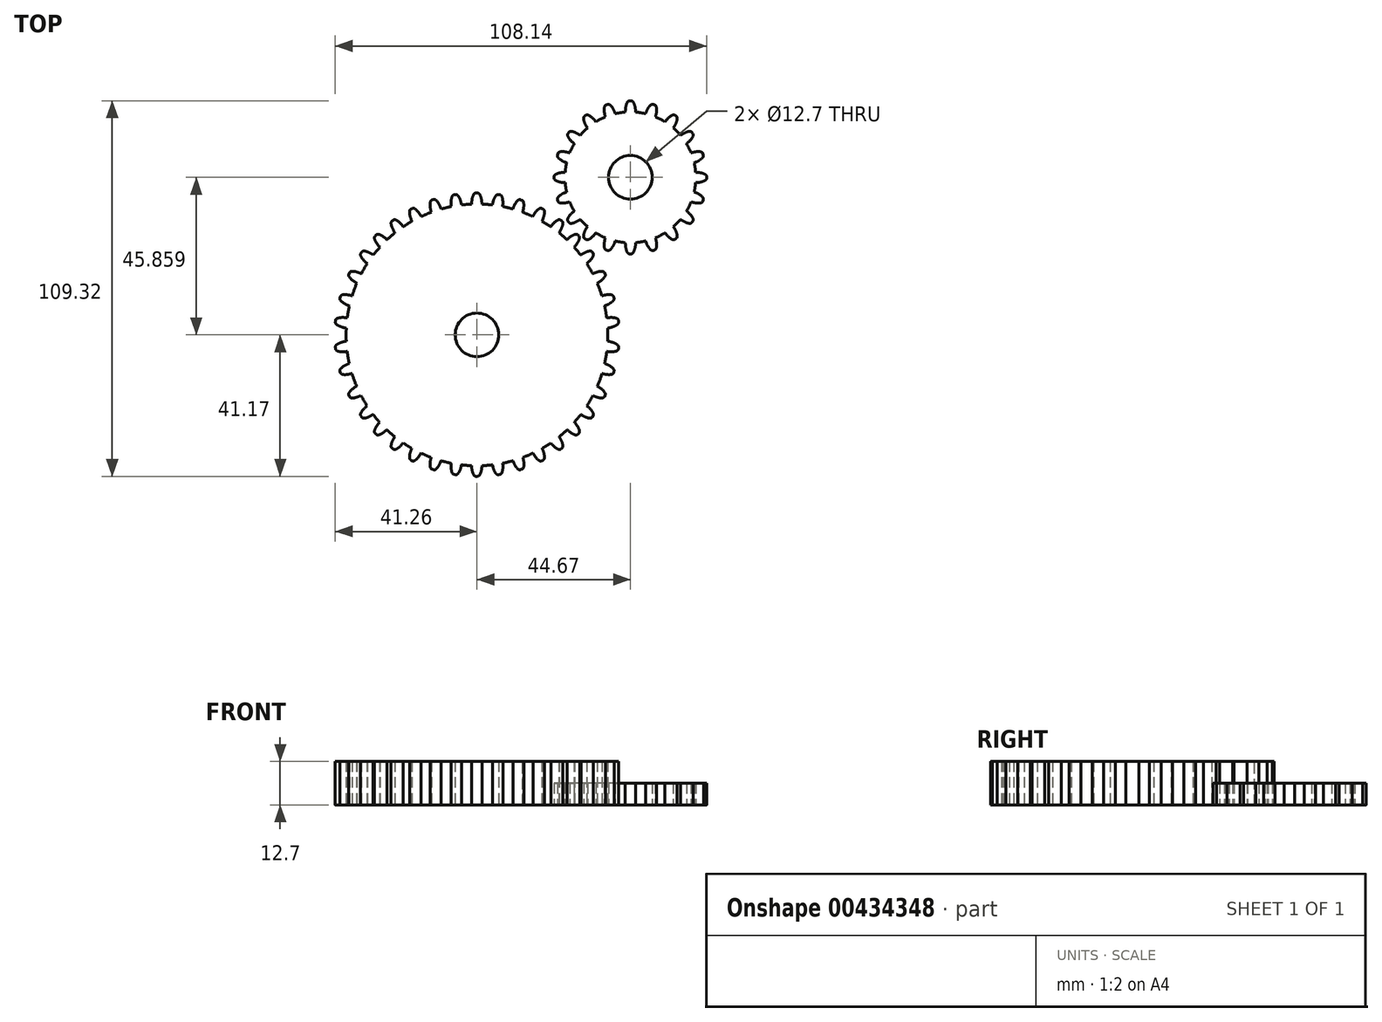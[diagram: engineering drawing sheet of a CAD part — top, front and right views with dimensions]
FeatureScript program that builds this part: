
annotation { "Feature Type Name" : "Feature", "Feature Type Description" : "" }
export const myFeature = defineFeature(function(context is Context, id is Id, definition is map)
    precondition{}
    {
        {
            var Q0;
            Q0=qCreatedBy(makeId("Top.planeOp"),FACE);
            var sketch = newSketch(context, id + "F0", { "sketchPlane" : qUnion([Q0])});
            skCircle(sketch, "E0", {"center": v(0, 0) * mm, "radius": 38.1 * mm});
            skCircle(sketch, "E1", {"center": v(0, 0) * mm, "radius": 6.35 * mm});
            skEllipticalArc(sketch, "E2", {});
            skLineSegment(sketch, "E3", {"start": v(12.68, 39.34) * mm, "end": v(13.04, 39.21) * mm});
            skPoint(sketch, "E4.visualSharp", {"position": v(12.33, 39.46) * mm});
            skPoint(sketch, "E5.visualSharp", {"position": v(13.37, 39.1) * mm});
            skArc(sketch, "E5.filletArc", {"start": v(13.53, 38.69) * mm, "mid": v(13.35, 39.01) * mm, "end": v(13.04, 39.21) * mm});
            skArc(sketch, "E6.filletArc", {"start": v(12.68, 39.34) * mm, "mid": v(12.29, 39.37) * mm, "end": v(11.94, 39.2) * mm});
            skLineSegment(sketch, "E7", {"start": v(10.43, 36.57) * mm, "end": v(13.3, 35.7) * mm});
            skEllipticalArc(sketch, "E8", {});
            skLineSegment(sketch, "E9", {"start": v(18.9, 36.8) * mm, "end": v(19.22, 36.63) * mm});
            skPoint(sketch, "E10.visualSharp", {"position": v(18.6, 36.96) * mm});
            skArc(sketch, "E11.filletArc", {"start": v(19.62, 36.05) * mm, "mid": v(19.5, 36.39) * mm, "end": v(19.22, 36.63) * mm});
            skArc(sketch, "E12.filletArc", {"start": v(18.9, 36.8) * mm, "mid": v(18.53, 36.89) * mm, "end": v(18.16, 36.78) * mm});
            skLineSegment(sketch, "E13", {"start": v(16.24, 34.4) * mm, "end": v(18.93, 33.1) * mm});
            skEllipticalArc(sketch, "E14", {});
            skLineSegment(sketch, "E15", {"start": v(24.42, 33.38) * mm, "end": v(24.72, 33.15) * mm});
            skPoint(sketch, "E16.visualSharp", {"position": v(24.12, 33.6) * mm});
            skPoint(sketch, "E17.visualSharp", {"position": v(25, 32.94) * mm});
            skArc(sketch, "E17.filletArc", {"start": v(25.02, 32.5) * mm, "mid": v(24.95, 32.87) * mm, "end": v(24.72, 33.15) * mm});
            skArc(sketch, "E18.filletArc", {"start": v(24.42, 33.38) * mm, "mid": v(24.05, 33.53) * mm, "end": v(23.67, 33.48) * mm});
            skLineSegment(sketch, "E19", {"start": v(21.43, 31.44) * mm, "end": v(23.88, 29.73) * mm});
            skEllipticalArc(sketch, "E20", {});
            skLineSegment(sketch, "E21", {"start": v(33.57, 24.1) * mm, "end": v(33.8, 23.79) * mm});
            skPoint(sketch, "E22.visualSharp", {"position": v(33.36, 24.4) * mm});
            skPoint(sketch, "E23.visualSharp", {"position": v(33.99, 23.5) * mm});
            skArc(sketch, "E23.filletArc", {"start": v(33.88, 23.08) * mm, "mid": v(33.92, 23.44) * mm, "end": v(33.8, 23.79) * mm});
            skArc(sketch, "E24.filletArc", {"start": v(33.57, 24.1) * mm, "mid": v(33.27, 24.35) * mm, "end": v(32.89, 24.42) * mm});
            skLineSegment(sketch, "E25", {"start": v(30.13, 23.18) * mm, "end": v(31.94, 20.79) * mm});
            skEllipticalArc(sketch, "E26", {});
            skLineSegment(sketch, "E27", {"start": v(37.13, 18.09) * mm, "end": v(37.3, 17.75) * mm});
            skPoint(sketch, "E28.visualSharp", {"position": v(36.97, 18.42) * mm});
            skPoint(sketch, "E29.visualSharp", {"position": v(37.45, 17.43) * mm});
            skArc(sketch, "E29.filletArc", {"start": v(37.28, 17.03) * mm, "mid": v(37.38, 17.38) * mm, "end": v(37.3, 17.75) * mm});
            skArc(sketch, "E30.filletArc", {"start": v(37.13, 18.09) * mm, "mid": v(36.88, 18.38) * mm, "end": v(36.5, 18.51) * mm});
            skLineSegment(sketch, "E31", {"start": v(33.59, 17.72) * mm, "end": v(35, 15.07) * mm});
            skEllipticalArc(sketch, "E32", {});
            skLineSegment(sketch, "E33", {"start": v(39.78, 11.13) * mm, "end": v(39.9, 10.77) * mm});
            skPoint(sketch, "E34.visualSharp", {"position": v(39.68, 11.48) * mm});
            skPoint(sketch, "E35.visualSharp", {"position": v(40, 10.44) * mm});
            skArc(sketch, "E35.filletArc", {"start": v(39.76, 10.07) * mm, "mid": v(39.91, 10.4) * mm, "end": v(39.9, 10.77) * mm});
            skArc(sketch, "E36.filletArc", {"start": v(39.78, 11.13) * mm, "mid": v(39.58, 11.47) * mm, "end": v(39.23, 11.65) * mm});
            skLineSegment(sketch, "E37", {"start": v(36.23, 11.32) * mm, "end": v(37.2, 8.49) * mm});
            skPoint(sketch, "E38.visualSharp", {"position": v(-45.71, -0.07) * mm});
            skPoint(sketch, "E39", {"position": v(4.52, 37.83) * mm});
            skEllipticalArc(sketch, "E40", {});
            skLineSegment(sketch, "E41", {"start": v(6.28, 40.86) * mm, "end": v(6.66, 40.8) * mm});
            skPoint(sketch, "E42.visualSharp", {"position": v(5.92, 40.93) * mm});
            skPoint(sketch, "E43.visualSharp", {"position": v(7, 40.74) * mm});
            skArc(sketch, "E43.filletArc", {"start": v(7.22, 40.36) * mm, "mid": v(7, 40.65) * mm, "end": v(6.66, 40.8) * mm});
            skArc(sketch, "E44.filletArc", {"start": v(6.28, 40.86) * mm, "mid": v(5.9, 40.83) * mm, "end": v(5.57, 40.6) * mm});
            skLineSegment(sketch, "E45", {"start": v(4.5, 37.78) * mm, "end": v(7.47, 37.37) * mm});
            skPoint(sketch, "E46", {"position": v(0, 38.1) * mm});
            skPoint(sketch, "E47", {"position": v(10.46, 36.63) * mm});
            skPoint(sketch, "E48", {"position": v(16.3, 34.44) * mm});
            skPoint(sketch, "E49", {"position": v(21.46, 31.48) * mm});
            skPoint(sketch, "E50", {"position": v(26.2, 27.67) * mm});
            skEllipticalArc(sketch, "E51", {});
            skLineSegment(sketch, "E52", {"start": v(29.4, 29.07) * mm, "end": v(29.66, 28.8) * mm});
            skPoint(sketch, "E53.visualSharp", {"position": v(29.14, 29.34) * mm});
            skPoint(sketch, "E54.visualSharp", {"position": v(29.9, 28.55) * mm});
            skArc(sketch, "E54.filletArc", {"start": v(29.86, 28.11) * mm, "mid": v(29.85, 28.48) * mm, "end": v(29.66, 28.8) * mm});
            skArc(sketch, "E55.filletArc", {"start": v(29.4, 29.07) * mm, "mid": v(29.06, 29.28) * mm, "end": v(28.67, 29.29) * mm});
            skLineSegment(sketch, "E56", {"start": v(26.14, 27.63) * mm, "end": v(28.3, 25.55) * mm});
            skPoint(sketch, "E57", {"position": v(30.2, 23.23) * mm});
            skPoint(sketch, "E58", {"position": v(33.7, 17.79) * mm});
            skPoint(sketch, "E59", {"position": v(36.14, 12.08) * mm});
            skPoint(sketch, "E60", {"position": v(37.7, 5.5) * mm});
            skEllipticalArc(sketch, "E61", {});
            skLineSegment(sketch, "E62", {"start": v(-0.26, 41.32) * mm, "end": v(0.12, 41.32) * mm});
            skPoint(sketch, "E63.visualSharp", {"position": v(-0.63, 41.33) * mm});
            skPoint(sketch, "E64.visualSharp", {"position": v(0.46, 41.31) * mm});
            skArc(sketch, "E64.filletArc", {"start": v(0.74, 40.97) * mm, "mid": v(0.47, 41.22) * mm, "end": v(0.12, 41.32) * mm});
            skArc(sketch, "E65.filletArc", {"start": v(-0.26, 41.32) * mm, "mid": v(-0.64, 41.23) * mm, "end": v(-0.93, 40.96) * mm});
            skLineSegment(sketch, "E66", {"start": v(-1.54, 38) * mm, "end": v(1.45, 38.05) * mm});
            skEllipticalArc(sketch, "E67", {});
            skLineSegment(sketch, "E68", {"start": v(41.2, 4.2) * mm, "end": v(41.25, 3.83) * mm});
            skPoint(sketch, "E69.visualSharp", {"position": v(41.14, 4.57) * mm});
            skPoint(sketch, "E70.visualSharp", {"position": v(41.3, 3.48) * mm});
            skArc(sketch, "E70.filletArc", {"start": v(41, 3.15) * mm, "mid": v(41.21, 3.46) * mm, "end": v(41.25, 3.83) * mm});
            skArc(sketch, "E71.filletArc", {"start": v(41.2, 4.2) * mm, "mid": v(41.04, 4.56) * mm, "end": v(40.73, 4.8) * mm});
            skLineSegment(sketch, "E72", {"start": v(37.71, 4.95) * mm, "end": v(38.23, 2) * mm});
            skEllipticalArc(sketch, "E73.MirrorCS", {});
            skArc(sketch, "E74.MirrorCS", {"start": v(6.28, -40.71) * mm, "mid": v(5.9, -40.68) * mm, "end": v(5.57, -40.46) * mm});
            skLineSegment(sketch, "E75.MirrorCS", {"start": v(6.28, -40.71) * mm, "end": v(6.66, -40.65) * mm});
            skArc(sketch, "E76.MirrorCS", {"start": v(7.22, -40.2) * mm, "mid": v(7, -40.5) * mm, "end": v(6.66, -40.65) * mm});
            skEllipticalArc(sketch, "E77.MirrorCS", {});
            skLineSegment(sketch, "E78.MirrorCS", {"start": v(-0.26, -41.17) * mm, "end": v(0.12, -41.17) * mm});
            skArc(sketch, "E79.MirrorCS", {"start": v(-0.26, -41.17) * mm, "mid": v(-0.64, -41.08) * mm, "end": v(-0.93, -40.8) * mm});
            skArc(sketch, "E80.MirrorCS", {"start": v(0.74, -40.82) * mm, "mid": v(0.47, -41.07) * mm, "end": v(0.12, -41.17) * mm});
            skEllipticalArc(sketch, "E81.MirrorCS", {});
            skArc(sketch, "E82.MirrorCS", {"start": v(12.7, -39.25) * mm, "mid": v(12.32, -39.28) * mm, "end": v(11.96, -39.11) * mm});
            skLineSegment(sketch, "E83.MirrorCS", {"start": v(12.7, -39.25) * mm, "end": v(13.07, -39.13) * mm});
            skArc(sketch, "E84.MirrorCS", {"start": v(13.55, -38.6) * mm, "mid": v(13.38, -38.93) * mm, "end": v(13.07, -39.13) * mm});
            skEllipticalArc(sketch, "E85.MirrorCS", {});
            skPoint(sketch, "E86.MirrorP", {"position": v(18.6, -36.81) * mm});
            skArc(sketch, "E87.MirrorCS", {"start": v(18.9, -36.65) * mm, "mid": v(18.53, -36.73) * mm, "end": v(18.16, -36.63) * mm});
            skLineSegment(sketch, "E88.MirrorCS", {"start": v(18.9, -36.65) * mm, "end": v(19.22, -36.48) * mm});
            skArc(sketch, "E89.MirrorCS", {"start": v(19.62, -35.9) * mm, "mid": v(19.5, -36.24) * mm, "end": v(19.22, -36.48) * mm});
            skEllipticalArc(sketch, "E90.MirrorCS", {});
            skArc(sketch, "E91.MirrorCS", {"start": v(24.42, -33.23) * mm, "mid": v(24.05, -33.38) * mm, "end": v(23.67, -33.33) * mm});
            skLineSegment(sketch, "E92.MirrorCS", {"start": v(24.42, -33.23) * mm, "end": v(24.72, -33) * mm});
            skPoint(sketch, "E93.MirrorP", {"position": v(25, -32.8) * mm});
            skArc(sketch, "E94.MirrorCS", {"start": v(25.02, -32.35) * mm, "mid": v(24.95, -32.71) * mm, "end": v(24.72, -33) * mm});
            skEllipticalArc(sketch, "E95.MirrorCS", {});
            skArc(sketch, "E96.MirrorCS", {"start": v(29.4, -28.92) * mm, "mid": v(29.06, -29.13) * mm, "end": v(28.67, -29.13) * mm});
            skLineSegment(sketch, "E97.MirrorCS", {"start": v(29.4, -28.92) * mm, "end": v(29.66, -28.65) * mm});
            skPoint(sketch, "E98.MirrorP", {"position": v(29.9, -28.4) * mm});
            skArc(sketch, "E99.MirrorCS", {"start": v(29.86, -27.96) * mm, "mid": v(29.85, -28.33) * mm, "end": v(29.66, -28.65) * mm});
            skEllipticalArc(sketch, "E100.MirrorCS", {});
            skArc(sketch, "E101.MirrorCS", {"start": v(33.57, -23.95) * mm, "mid": v(33.27, -24.2) * mm, "end": v(32.89, -24.27) * mm});
            skLineSegment(sketch, "E102.MirrorCS", {"start": v(33.57, -23.95) * mm, "end": v(33.8, -23.63) * mm});
            skPoint(sketch, "E103.MirrorP", {"position": v(33.99, -23.35) * mm});
            skArc(sketch, "E104.MirrorCS", {"start": v(33.88, -22.92) * mm, "mid": v(33.92, -23.3) * mm, "end": v(33.8, -23.63) * mm});
            skLineSegment(sketch, "E105.MirrorCS", {"start": v(37.13, -17.94) * mm, "end": v(37.3, -17.6) * mm});
            skArc(sketch, "E106.MirrorCS", {"start": v(37.13, -17.94) * mm, "mid": v(36.88, -18.23) * mm, "end": v(36.5, -18.36) * mm});
            skEllipticalArc(sketch, "E107.MirrorCS", {});
            skPoint(sketch, "E108.MirrorP", {"position": v(37.45, -17.28) * mm});
            skArc(sketch, "E109.MirrorCS", {"start": v(37.28, -16.88) * mm, "mid": v(37.38, -17.23) * mm, "end": v(37.3, -17.6) * mm});
            skEllipticalArc(sketch, "E110.MirrorCS", {});
            skArc(sketch, "E111.MirrorCS", {"start": v(39.78, -10.98) * mm, "mid": v(39.58, -11.31) * mm, "end": v(39.23, -11.5) * mm});
            skLineSegment(sketch, "E112.MirrorCS", {"start": v(39.78, -10.98) * mm, "end": v(39.9, -10.62) * mm});
            skArc(sketch, "E113.MirrorCS", {"start": v(39.76, -9.91) * mm, "mid": v(39.91, -10.25) * mm, "end": v(39.9, -10.62) * mm});
            skArc(sketch, "E114.MirrorCS", {"start": v(41, -3) * mm, "mid": v(41.21, -3.3) * mm, "end": v(41.25, -3.68) * mm});
            skArc(sketch, "E115.MirrorCS", {"start": v(41.2, -4.05) * mm, "mid": v(41.04, -4.41) * mm, "end": v(40.73, -4.65) * mm});
            skLineSegment(sketch, "E116.MirrorCS", {"start": v(41.2, -4.05) * mm, "end": v(41.25, -3.68) * mm});
            skEllipticalArc(sketch, "E117.MirrorCS", {});
            skEllipticalArc(sketch, "E118.MirrorCS", {});
            skArc(sketch, "E119.MirrorCS", {"start": v(-6.28, -40.71) * mm, "mid": v(-5.9, -40.68) * mm, "end": v(-5.57, -40.46) * mm});
            skArc(sketch, "E120.MirrorCS", {"start": v(-7.22, -40.2) * mm, "mid": v(-7, -40.5) * mm, "end": v(-6.66, -40.65) * mm});
            skLineSegment(sketch, "E121.MirrorCS", {"start": v(-6.28, -40.71) * mm, "end": v(-6.66, -40.65) * mm});
            skEllipticalArc(sketch, "E122.MirrorCS", {});
            skArc(sketch, "E123.MirrorCS", {"start": v(-13.55, -38.6) * mm, "mid": v(-13.38, -38.93) * mm, "end": v(-13.07, -39.13) * mm});
            skArc(sketch, "E124.MirrorCS", {"start": v(-12.7, -39.25) * mm, "mid": v(-12.32, -39.28) * mm, "end": v(-11.96, -39.11) * mm});
            skLineSegment(sketch, "E125.MirrorCS", {"start": v(-12.7, -39.25) * mm, "end": v(-13.07, -39.13) * mm});
            skEllipticalArc(sketch, "E126.MirrorCS", {});
            skArc(sketch, "E127.MirrorCS", {"start": v(-19.62, -35.9) * mm, "mid": v(-19.5, -36.24) * mm, "end": v(-19.22, -36.48) * mm});
            skArc(sketch, "E128.MirrorCS", {"start": v(-18.9, -36.65) * mm, "mid": v(-18.53, -36.73) * mm, "end": v(-18.16, -36.63) * mm});
            skLineSegment(sketch, "E129.MirrorCS", {"start": v(-18.9, -36.65) * mm, "end": v(-19.22, -36.48) * mm});
            skEllipticalArc(sketch, "E130.MirrorCS", {});
            skArc(sketch, "E131.MirrorCS", {"start": v(-25.02, -32.35) * mm, "mid": v(-24.95, -32.71) * mm, "end": v(-24.72, -33) * mm});
            skArc(sketch, "E132.MirrorCS", {"start": v(-24.42, -33.23) * mm, "mid": v(-24.05, -33.38) * mm, "end": v(-23.67, -33.33) * mm});
            skLineSegment(sketch, "E133.MirrorCS", {"start": v(-24.42, -33.23) * mm, "end": v(-24.72, -33) * mm});
            skEllipticalArc(sketch, "E134.MirrorCS", {});
            skArc(sketch, "E135.MirrorCS", {"start": v(-29.86, -27.96) * mm, "mid": v(-29.85, -28.33) * mm, "end": v(-29.66, -28.65) * mm});
            skArc(sketch, "E136.MirrorCS", {"start": v(-29.4, -28.92) * mm, "mid": v(-29.06, -29.13) * mm, "end": v(-28.67, -29.13) * mm});
            skLineSegment(sketch, "E137.MirrorCS", {"start": v(-29.4, -28.92) * mm, "end": v(-29.66, -28.65) * mm});
            skEllipticalArc(sketch, "E138.MirrorCS", {});
            skArc(sketch, "E139.MirrorCS", {"start": v(-33.88, -22.92) * mm, "mid": v(-33.92, -23.3) * mm, "end": v(-33.8, -23.63) * mm});
            skArc(sketch, "E140.MirrorCS", {"start": v(-33.57, -23.95) * mm, "mid": v(-33.27, -24.2) * mm, "end": v(-32.89, -24.27) * mm});
            skLineSegment(sketch, "E141.MirrorCS", {"start": v(-33.57, -23.95) * mm, "end": v(-33.8, -23.63) * mm});
            skEllipticalArc(sketch, "E142.MirrorCS", {});
            skArc(sketch, "E143.MirrorCS", {"start": v(-37.28, -16.88) * mm, "mid": v(-37.38, -17.23) * mm, "end": v(-37.3, -17.6) * mm});
            skArc(sketch, "E144.MirrorCS", {"start": v(-37.13, -17.94) * mm, "mid": v(-36.88, -18.23) * mm, "end": v(-36.5, -18.36) * mm});
            skLineSegment(sketch, "E145.MirrorCS", {"start": v(-37.13, -17.94) * mm, "end": v(-37.3, -17.6) * mm});
            skEllipticalArc(sketch, "E146.MirrorCS", {});
            skArc(sketch, "E147.MirrorCS", {"start": v(-39.78, -10.98) * mm, "mid": v(-39.58, -11.31) * mm, "end": v(-39.23, -11.5) * mm});
            skArc(sketch, "E148.MirrorCS", {"start": v(-39.76, -9.91) * mm, "mid": v(-39.91, -10.25) * mm, "end": v(-39.9, -10.62) * mm});
            skEllipticalArc(sketch, "E149.MirrorCS", {});
            skArc(sketch, "E150.MirrorCS", {"start": v(-41.2, -4.05) * mm, "mid": v(-41.04, -4.41) * mm, "end": v(-40.73, -4.65) * mm});
            skLineSegment(sketch, "E151.MirrorCS", {"start": v(-41.2, -4.05) * mm, "end": v(-41.25, -3.68) * mm});
            skArc(sketch, "E152.MirrorCS", {"start": v(-41, -3) * mm, "mid": v(-41.21, -3.3) * mm, "end": v(-41.25, -3.68) * mm});
            skEllipticalArc(sketch, "E153.MirrorCS", {});
            skPoint(sketch, "E154.MirrorP", {"position": v(-41.3, 3.48) * mm});
            skArc(sketch, "E155.MirrorCS", {"start": v(-41, 3.15) * mm, "mid": v(-41.21, 3.46) * mm, "end": v(-41.25, 3.83) * mm});
            skLineSegment(sketch, "E156.MirrorCS", {"start": v(-41.2, 4.2) * mm, "end": v(-41.25, 3.83) * mm});
            skArc(sketch, "E157.MirrorCS", {"start": v(-41.2, 4.2) * mm, "mid": v(-41.04, 4.56) * mm, "end": v(-40.73, 4.8) * mm});
            skEllipticalArc(sketch, "E158.MirrorCS", {});
            skArc(sketch, "E159.MirrorCS", {"start": v(-39.76, 10.07) * mm, "mid": v(-39.91, 10.4) * mm, "end": v(-39.9, 10.77) * mm});
            skLineSegment(sketch, "E160.MirrorCS", {"start": v(-39.78, 11.13) * mm, "end": v(-39.9, 10.77) * mm});
            skArc(sketch, "E161.MirrorCS", {"start": v(-39.78, 11.13) * mm, "mid": v(-39.58, 11.47) * mm, "end": v(-39.23, 11.65) * mm});
            skEllipticalArc(sketch, "E162.MirrorCS", {});
            skArc(sketch, "E163.MirrorCS", {"start": v(-37.28, 17.03) * mm, "mid": v(-37.38, 17.38) * mm, "end": v(-37.3, 17.75) * mm});
            skLineSegment(sketch, "E164.MirrorCS", {"start": v(-37.13, 18.09) * mm, "end": v(-37.3, 17.75) * mm});
            skArc(sketch, "E165.MirrorCS", {"start": v(-37.13, 18.09) * mm, "mid": v(-36.88, 18.38) * mm, "end": v(-36.5, 18.51) * mm});
            skEllipticalArc(sketch, "E166.MirrorCS", {});
            skArc(sketch, "E167.MirrorCS", {"start": v(-33.88, 23.08) * mm, "mid": v(-33.92, 23.44) * mm, "end": v(-33.8, 23.79) * mm});
            skLineSegment(sketch, "E168.MirrorCS", {"start": v(-33.57, 24.1) * mm, "end": v(-33.8, 23.79) * mm});
            skArc(sketch, "E169.MirrorCS", {"start": v(-33.57, 24.1) * mm, "mid": v(-33.27, 24.35) * mm, "end": v(-32.89, 24.42) * mm});
            skEllipticalArc(sketch, "E170.MirrorCS", {});
            skArc(sketch, "E171.MirrorCS", {"start": v(-29.86, 28.11) * mm, "mid": v(-29.85, 28.48) * mm, "end": v(-29.66, 28.8) * mm});
            skLineSegment(sketch, "E172.MirrorCS", {"start": v(-29.4, 29.07) * mm, "end": v(-29.66, 28.8) * mm});
            skArc(sketch, "E173.MirrorCS", {"start": v(-29.4, 29.07) * mm, "mid": v(-29.06, 29.28) * mm, "end": v(-28.67, 29.29) * mm});
            skEllipticalArc(sketch, "E174.MirrorCS", {});
            skArc(sketch, "E175.MirrorCS", {"start": v(-25.02, 32.5) * mm, "mid": v(-24.95, 32.87) * mm, "end": v(-24.72, 33.15) * mm});
            skLineSegment(sketch, "E176.MirrorCS", {"start": v(-24.42, 33.38) * mm, "end": v(-24.72, 33.15) * mm});
            skArc(sketch, "E177.MirrorCS", {"start": v(-24.42, 33.38) * mm, "mid": v(-24.05, 33.53) * mm, "end": v(-23.67, 33.48) * mm});
            skEllipticalArc(sketch, "E178.MirrorCS", {});
            skArc(sketch, "E179.MirrorCS", {"start": v(-19.62, 36.05) * mm, "mid": v(-19.5, 36.39) * mm, "end": v(-19.22, 36.63) * mm});
            skLineSegment(sketch, "E180.MirrorCS", {"start": v(-18.9, 36.8) * mm, "end": v(-19.22, 36.63) * mm});
            skArc(sketch, "E181.MirrorCS", {"start": v(-18.9, 36.8) * mm, "mid": v(-18.53, 36.89) * mm, "end": v(-18.16, 36.78) * mm});
            skEllipticalArc(sketch, "E182.MirrorCS", {});
            skArc(sketch, "E183.MirrorCS", {"start": v(-13.55, 38.76) * mm, "mid": v(-13.38, 39.08) * mm, "end": v(-13.07, 39.28) * mm});
            skLineSegment(sketch, "E184.MirrorCS", {"start": v(-12.7, 39.4) * mm, "end": v(-13.07, 39.28) * mm});
            skArc(sketch, "E185.MirrorCS", {"start": v(-12.7, 39.4) * mm, "mid": v(-12.32, 39.43) * mm, "end": v(-11.96, 39.26) * mm});
            skEllipticalArc(sketch, "E186.MirrorCS", {});
            skArc(sketch, "E187.MirrorCS", {"start": v(-7.22, 40.36) * mm, "mid": v(-7, 40.65) * mm, "end": v(-6.66, 40.8) * mm});
            skLineSegment(sketch, "E188.MirrorCS", {"start": v(-6.28, 40.86) * mm, "end": v(-6.66, 40.8) * mm});
            skArc(sketch, "E189.MirrorCS", {"start": v(-6.28, 40.86) * mm, "mid": v(-5.9, 40.83) * mm, "end": v(-5.57, 40.6) * mm});
            skLineSegment(sketch, "E190", {"start": v(-39.9, -10.62) * mm, "end": v(-39.78, -10.98) * mm});
            const initialGuessF0  = {"E2": [0.01186746590526298, 0.036133459957926904, 0.9565221208926966, -0.29165978852583985, 0.0014986000688646897, 0.0035390805472536617, 2.1566096616366126, 0.9748157687295604], "E8": [0.017585702386777147, 0.03374703845333271, 0.8991201033352045, -0.4377019988285309, 0.0014986000000007816, 0.003539080620550978, 2.1409023225018835, 0.9908088013620491], "E14": [0.02265578287977473, 0.03058570050431115, 0.819578764825096, -0.5729665332702865, 0.0014985999999604874, 0.0035390806203384963, 2.156609722361633, 0.974815710010029], "E20": [0.031033398799110372, 0.021983045095617812, 0.6024093289154265, -0.7981873216455305, 0.0014986000000000005, 0.0035390806205390707, 2.1566097223429517, 0.974815710028964], "E26": [0.034294476878703864, 0.01639607277429761, 0.4701286637719916, -0.8825978923042824, 0.0014986000000000005, 0.0035390806205390707, 2.1566097223429397, 0.9748157100289685], "E32": [0.036714569503235456, 0.009905693299014778, 0.32627187065891905, -0.9452759736800305, 0.0014985999847553029, 0.003539080625213695, 2.1566097285726453, 0.9748157042875452], "E40": [0.005982244381583665, 0.03757325514283656, 0.9903713893188204, -0.13843594626652975, 0.0014985999999950434, 0.0035390806205121863, 2.156609722345128, 0.9748157100267223], "E51": [0.02722062515224479, 0.026587915261583314, 0.7198566770990191, -0.6941227300960245, 0.0014985999999683702, 0.003539080620359171, 2.1566097223570546, 0.9748157100144512], "E61": [-4.473054053318043e-05, 0.03802693754338048, 0.99983442728575, 0.018196648432512064, 0.0014986000000000983, 0.0035390806205391036, 2.156609722343001, 0.9748157100289072], "E67": [0.03797341145007212, 0.003471938573619611, 0.1743811812559528, -0.9846782233926872, 0.0014985999999967946, 0.003539080620539968, 2.15660972234474, 0.9748157100274488], "E73.MirrorCS": [0.005982244381583665, -0.037421951624719965, 0.9903713893188204, 0.13843594626652975, 0.0014985999999950434, 0.0035390806205121863, 5.308369597152864, 4.126575584834459], "E77.MirrorCS": [-4.473054053318043e-05, -0.037875634025263887, 0.99983442728575, -0.018196648432512064, 0.0014986000000000983, 0.0035390806205391036, 5.308369597150679, 4.126575584836585], "E81.MirrorCS": [0.011894871004150282, -0.03605066825344335, 0.9565221208926966, 0.29165978852583985, 0.0014985999999839522, 0.0035390806204531537, 5.3083695971582525, 4.126575584829374], "E85.MirrorCS": [0.017585702386777147, -0.033595734935216115, 0.8991201033352045, 0.4377019988285309, 0.0014986000000007816, 0.003539080620550978, 5.292376505817537, 4.142282984677703], "E85.MirrorCS": [0.017585702386777147, -0.033595734935216115, 0.8991201033352045, 0.4377019988285309, 0.0014986000000007816, 0.003539080620550978, 5.292376505817537, 4.142282984677703], "E85.MirrorCS": [0.017585702386777147, -0.033595734935216115, 0.8991201033352045, 0.4377019988285309, 0.0014986000000007816, 0.003539080620550978, 5.292376505817537, 4.142282984677703], "E90.MirrorCS": [0.02265578287977473, -0.030434396986194552, 0.819578764825096, 0.5729665332702865, 0.0014985999999604874, 0.0035390806203384963, 5.308369597169592, 4.126575584817891], "E95.MirrorCS": [0.0272206251522448, -0.02643661174346671, 0.7198566770990189, 0.6941227300960248, 0.0014985999999683702, 0.003539080620359171, 5.308369597165132, 4.126575584822529], "E100.MirrorCS": [0.031033398799110372, -0.021831741577501215, 0.6024093289154265, 0.7981873216455305, 0.0014986000000000005, 0.0035390806205390707, 5.308369597150622, 4.126575584836635], "E107.MirrorCS": [0.034294476878703864, -0.016244769256181013, 0.4701286637719916, 0.8825978923042824, 0.0014986000000000005, 0.0035390806205390707, 5.308369597150618, 4.1265755848366465], "E110.MirrorCS": [0.036714569503235456, -0.009754389780898182, 0.32627187065891905, 0.9452759736800305, 0.0014985999847553029, 0.003539080625213695, 5.308369602892046, 4.126575578606946], "E117.MirrorCS": [0.03797341145007212, -0.0033206350555030125, 0.1743811812559528, 0.9846782233926872, 0.0014985999999967946, 0.003539080620539968, 5.308369597152129, 4.126575584834848], "E117.MirrorCS": [0.03797341145007212, -0.0033206350555030125, 0.1743811812559528, 0.9846782233926872, 0.0014985999999967946, 0.003539080620539968, 5.308369597152129, 4.126575584834848], "E118.MirrorCS": [-0.005982244381583665, -0.037421951624719965, -0.9903713893188204, 0.13843594626652975, 0.0014985999999950434, 0.0035390806205121863, 2.1566097223451273, 0.9748157100267223], "E122.MirrorCS": [-0.011894871004150282, -0.03605066825344335, -0.9565221208926966, 0.29165978852583985, 0.0014985999999839522, 0.0035390806204531537, 2.156609722350213, 0.9748157100213337], "E126.MirrorCS": [-0.017585702386777147, -0.033595734935216115, -0.8991201033352045, 0.4377019988285309, 0.0014986000000007816, 0.003539080620550978, 2.1409023225018835, 0.9908088013620491], "E130.MirrorCS": [-0.02265578287977473, -0.030434396986194552, -0.819578764825096, 0.5729665332702865, 0.0014985999999604874, 0.0035390806203384963, 2.1566097223616953, 0.9748157100099935], "E134.MirrorCS": [-0.0272206251522448, -0.02643661174346671, -0.7198566770990189, 0.6941227300960248, 0.0014985999999683702, 0.003539080620359171, 2.156609722357058, 0.9748157100144548], "E138.MirrorCS": [-0.031033398799110372, -0.021831741577501215, -0.6024093289154265, 0.7981873216455305, 0.0014986000000000005, 0.0035390806205390707, 2.1566097223429512, 0.974815710028964], "E142.MirrorCS": [-0.034294476878703864, -0.016244769256181013, -0.4701286637719916, 0.8825978923042824, 0.0014986000000000005, 0.0035390806205390707, 2.1566097223429397, 0.9748157100289685], "E146.MirrorCS": [-0.036714569503235456, -0.009754389780898182, -0.32627187065891905, 0.9452759736800305, 0.0014985999847553029, 0.003539080625213695, 2.156609728572639, 0.9748157042875407], "E149.MirrorCS": [-0.03797341145007212, -0.0033206350555030125, -0.1743811812559528, 0.9846782233926872, 0.0014985999999967946, 0.003539080620539968, 2.1566097223447365, 0.9748157100274568], "E153.MirrorCS": [-0.03797341145007212, 0.003471938573619611, -0.1743811812559528, -0.9846782233926872, 0.0014985999999967946, 0.003539080620539968, 5.308369597152129, 4.12657558483485], "E158.MirrorCS": [-0.036714569503235456, 0.009905693299014778, -0.32627187065891905, -0.9452759736800305, 0.0014985999847553029, 0.003539080625213695, 5.308369602892045, 4.1265755786069445], "E162.MirrorCS": [-0.034294476878703864, 0.01639607277429761, -0.4701286637719916, -0.8825978923042824, 0.0014986000000000005, 0.0035390806205390707, 5.308369597150618, 4.1265755848366465], "E166.MirrorCS": [-0.031033398799110372, 0.021983045095617812, -0.6024093289154265, -0.7981873216455305, 0.0014986000000000005, 0.0035390806205390707, 5.308369597150622, 4.126575584836635], "E170.MirrorCS": [-0.02722062515224479, 0.026587915261583314, -0.7198566770990191, -0.6941227300960245, 0.0014985999999683702, 0.003539080620359171, 5.308369597165135, 4.126575584822532], "E174.MirrorCS": [-0.02265578287977473, 0.03058570050431115, -0.819578764825096, -0.5729665332702865, 0.0014985999999604874, 0.0035390806203384963, 5.308369597169592, 4.126575584817891], "E178.MirrorCS": [-0.017585702386777147, 0.03374703845333271, -0.8991201033352045, -0.4377019988285309, 0.0014986000000007816, 0.003539080620550978, 5.292376505817537, 4.142282984677703], "E182.MirrorCS": [-0.011894871004150282, 0.03620197177155995, -0.9565221208926966, -0.29165978852583985, 0.0014985999999839522, 0.0035390806204531537, 5.3083695971582525, 4.126575584829374], "E186.MirrorCS": [-0.005982244381583665, 0.03757325514283656, -0.9903713893188204, -0.13843594626652975, 0.0014985999999950434, 0.0035390806205121863, 5.308369597152864, 4.126575584834459]};
            skSetInitialGuess(sketch, initialGuessF0);
            skSolve(sketch);
        }
        {
            var Q0;
            Q0 = qSketchRegion(id + "F0", true);
            extrude(context, id + "F1", {"entities" : qUnion([Q0]), "depth" : 12.7 * mm});
        }
        {
            var Q0;
            Q0=qCreatedBy(makeId("Top.planeOp"),FACE);
            var sketch = newSketch(context, id + "F2", { "sketchPlane" : qUnion([Q0])});
            skCircle(sketch, "E191", {"center": v(44.67, 45.86) * mm, "radius": 19.05 * mm});
            skCircle(sketch, "E192", {"center": v(44.67, 45.86) * mm, "radius": 6.35 * mm});
            skEllipticalArc(sketch, "E193", {});
            skLineSegment(sketch, "E194", {"start": v(44.48, 68.15) * mm, "end": v(44.86, 68.14) * mm});
            skPoint(sketch, "E195.visualSharp", {"position": v(44.11, 68.16) * mm});
            skPoint(sketch, "E196.visualSharp", {"position": v(45.2, 68.14) * mm});
            skArc(sketch, "E196.filletArc", {"start": v(45.49, 67.8) * mm, "mid": v(45.22, 68.05) * mm, "end": v(44.86, 68.14) * mm});
            skArc(sketch, "E197.filletArc", {"start": v(44.48, 68.15) * mm, "mid": v(44.1, 68.06) * mm, "end": v(43.82, 67.79) * mm});
            skLineSegment(sketch, "E198", {"start": v(43.2, 64.83) * mm, "end": v(46.2, 64.88) * mm});
            skEllipticalArc(sketch, "E199", {});
            skLineSegment(sketch, "E200", {"start": v(51.34, 67.11) * mm, "end": v(51.7, 66.99) * mm});
            skPoint(sketch, "E201.visualSharp", {"position": v(51, 67.23) * mm});
            skPoint(sketch, "E202.visualSharp", {"position": v(52.03, 66.88) * mm});
            skArc(sketch, "E202.filletArc", {"start": v(52.19, 66.47) * mm, "mid": v(52.01, 66.79) * mm, "end": v(51.7, 66.99) * mm});
            skArc(sketch, "E203.filletArc", {"start": v(51.34, 67.11) * mm, "mid": v(50.95, 67.14) * mm, "end": v(50.6, 66.97) * mm});
            skLineSegment(sketch, "E204", {"start": v(49.1, 64.35) * mm, "end": v(51.96, 63.47) * mm});
            skEllipticalArc(sketch, "E205", {});
            skLineSegment(sketch, "E206", {"start": v(57.7, 63.9) * mm, "end": v(58, 63.67) * mm});
            skPoint(sketch, "E207.visualSharp", {"position": v(57.41, 64.12) * mm});
            skPoint(sketch, "E208.visualSharp", {"position": v(58.29, 63.46) * mm});
            skArc(sketch, "E208.filletArc", {"start": v(58.31, 63.02) * mm, "mid": v(58.24, 63.38) * mm, "end": v(58, 63.67) * mm});
            skArc(sketch, "E209.filletArc", {"start": v(57.7, 63.9) * mm, "mid": v(57.34, 64.05) * mm, "end": v(56.95, 64) * mm});
            skLineSegment(sketch, "E210", {"start": v(54.72, 61.96) * mm, "end": v(57.17, 60.24) * mm});
            skEllipticalArc(sketch, "E211", {});
            skLineSegment(sketch, "E212", {"start": v(65.8, 52.77) * mm, "end": v(65.9, 52.4) * mm});
            skPoint(sketch, "E213.visualSharp", {"position": v(65.69, 53.12) * mm});
            skPoint(sketch, "E214.visualSharp", {"position": v(66.01, 52.08) * mm});
            skArc(sketch, "E214.filletArc", {"start": v(65.78, 51.7) * mm, "mid": v(65.93, 52.04) * mm, "end": v(65.9, 52.4) * mm});
            skArc(sketch, "E215.filletArc", {"start": v(65.8, 52.77) * mm, "mid": v(65.59, 53.1) * mm, "end": v(65.24, 53.29) * mm});
            skLineSegment(sketch, "E216", {"start": v(62.24, 52.94) * mm, "end": v(63.23, 50.12) * mm});
            skPoint(sketch, "E217", {"position": v(49.2, 64.68) * mm});
            skPoint(sketch, "E218", {"position": v(54.96, 62.3) * mm});
            skPoint(sketch, "E219", {"position": v(59.4, 58.24) * mm});
            skPoint(sketch, "E220", {"position": v(62.5, 53) * mm});
            skEllipticalArc(sketch, "E221", {});
            skLineSegment(sketch, "E222", {"start": v(66.88, 46.03) * mm, "end": v(66.88, 45.65) * mm});
            skPoint(sketch, "E223.visualSharp", {"position": v(66.89, 46.4) * mm});
            skPoint(sketch, "E224.visualSharp", {"position": v(66.87, 45.3) * mm});
            skArc(sketch, "E224.filletArc", {"start": v(66.53, 45.03) * mm, "mid": v(66.78, 45.3) * mm, "end": v(66.88, 45.65) * mm});
            skArc(sketch, "E225.filletArc", {"start": v(66.88, 46.03) * mm, "mid": v(66.79, 46.41) * mm, "end": v(66.52, 46.7) * mm});
            skLineSegment(sketch, "E226", {"start": v(63.56, 47.31) * mm, "end": v(63.61, 44.32) * mm});
            skEllipticalArc(sketch, "E227.MirrorCS", {});
            skArc(sketch, "E228.MirrorCS", {"start": v(65.78, 40.01) * mm, "mid": v(65.93, 39.68) * mm, "end": v(65.9, 39.31) * mm});
            skLineSegment(sketch, "E229.MirrorCS", {"start": v(65.8, 38.95) * mm, "end": v(65.9, 39.31) * mm});
            skArc(sketch, "E230.MirrorCS", {"start": v(65.8, 38.95) * mm, "mid": v(65.59, 38.62) * mm, "end": v(65.24, 38.43) * mm});
            skEllipticalArc(sketch, "E231.MirrorCS", {});
            skPoint(sketch, "E232.MirrorP", {"position": v(38.35, 67.23) * mm});
            skArc(sketch, "E233.MirrorCS", {"start": v(38, 67.11) * mm, "mid": v(38.39, 67.14) * mm, "end": v(38.74, 66.97) * mm});
            skLineSegment(sketch, "E234.MirrorCS", {"start": v(38, 67.11) * mm, "end": v(37.64, 66.99) * mm});
            skArc(sketch, "E235.MirrorCS", {"start": v(37.15, 66.47) * mm, "mid": v(37.33, 66.79) * mm, "end": v(37.64, 66.99) * mm});
            skEllipticalArc(sketch, "E236.MirrorCS", {});
            skArc(sketch, "E237.MirrorCS", {"start": v(31.64, 63.9) * mm, "mid": v(32, 64.05) * mm, "end": v(32.39, 64) * mm});
            skEllipticalArc(sketch, "E238.MirrorCS", {});
            skArc(sketch, "E239.MirrorCS", {"start": v(58.31, 28.7) * mm, "mid": v(58.24, 28.34) * mm, "end": v(58, 28.05) * mm});
            skLineSegment(sketch, "E240.MirrorCS", {"start": v(31.64, 63.9) * mm, "end": v(31.33, 63.67) * mm});
            skLineSegment(sketch, "E241.MirrorCS", {"start": v(57.7, 27.82) * mm, "end": v(58, 28.05) * mm});
            skArc(sketch, "E242.MirrorCS", {"start": v(31.03, 63.02) * mm, "mid": v(31.1, 63.38) * mm, "end": v(31.33, 63.67) * mm});
            skArc(sketch, "E243.MirrorCS", {"start": v(57.7, 27.82) * mm, "mid": v(57.34, 27.67) * mm, "end": v(56.95, 27.73) * mm});
            skEllipticalArc(sketch, "E244.MirrorCS", {});
            skArc(sketch, "E245.MirrorCS", {"start": v(52.19, 25.25) * mm, "mid": v(52.01, 24.93) * mm, "end": v(51.7, 24.73) * mm});
            skLineSegment(sketch, "E246.MirrorCS", {"start": v(51.34, 24.6) * mm, "end": v(51.7, 24.73) * mm});
            skArc(sketch, "E247.MirrorCS", {"start": v(51.34, 24.6) * mm, "mid": v(50.95, 24.58) * mm, "end": v(50.6, 24.75) * mm});
            skEllipticalArc(sketch, "E248.MirrorCS", {});
            skPoint(sketch, "E249.MirrorP", {"position": v(23.33, 52.08) * mm});
            skArc(sketch, "E250.MirrorCS", {"start": v(23.56, 51.7) * mm, "mid": v(23.4, 52.04) * mm, "end": v(23.43, 52.4) * mm});
            skLineSegment(sketch, "E251.MirrorCS", {"start": v(23.54, 52.77) * mm, "end": v(23.43, 52.4) * mm});
            skArc(sketch, "E252.MirrorCS", {"start": v(23.54, 52.77) * mm, "mid": v(23.75, 53.1) * mm, "end": v(24.1, 53.29) * mm});
            skEllipticalArc(sketch, "E253.MirrorCS", {});
            skArc(sketch, "E254.MirrorCS", {"start": v(22.81, 45.03) * mm, "mid": v(22.56, 45.3) * mm, "end": v(22.46, 45.65) * mm});
            skLineSegment(sketch, "E255.MirrorCS", {"start": v(22.46, 46.03) * mm, "end": v(22.46, 45.65) * mm});
            skArc(sketch, "E256.MirrorCS", {"start": v(22.46, 46.03) * mm, "mid": v(22.55, 46.41) * mm, "end": v(22.82, 46.7) * mm});
            skEllipticalArc(sketch, "E257.MirrorCS", {});
            skArc(sketch, "E258.MirrorCS", {"start": v(44.48, 23.57) * mm, "mid": v(44.1, 23.66) * mm, "end": v(43.82, 23.93) * mm});
            skLineSegment(sketch, "E259.MirrorCS", {"start": v(44.48, 23.57) * mm, "end": v(44.86, 23.58) * mm});
            skArc(sketch, "E260.MirrorCS", {"start": v(45.49, 23.92) * mm, "mid": v(45.22, 23.67) * mm, "end": v(44.86, 23.58) * mm});
            skEllipticalArc(sketch, "E261.MirrorCS", {});
            skArc(sketch, "E262.MirrorCS", {"start": v(38, 24.6) * mm, "mid": v(38.39, 24.58) * mm, "end": v(38.74, 24.75) * mm});
            skLineSegment(sketch, "E263.MirrorCS", {"start": v(38, 24.6) * mm, "end": v(37.64, 24.73) * mm});
            skArc(sketch, "E264.MirrorCS", {"start": v(37.15, 25.25) * mm, "mid": v(37.33, 24.93) * mm, "end": v(37.64, 24.73) * mm});
            skEllipticalArc(sketch, "E265.MirrorCS", {});
            skArc(sketch, "E266.MirrorCS", {"start": v(31.03, 28.7) * mm, "mid": v(31.1, 28.34) * mm, "end": v(31.33, 28.05) * mm});
            skLineSegment(sketch, "E267.MirrorCS", {"start": v(31.64, 27.82) * mm, "end": v(31.33, 28.05) * mm});
            skArc(sketch, "E268.MirrorCS", {"start": v(31.64, 27.82) * mm, "mid": v(32, 27.67) * mm, "end": v(32.39, 27.73) * mm});
            skEllipticalArc(sketch, "E269", {});
            skLineSegment(sketch, "E270", {"start": v(62.63, 58.95) * mm, "end": v(62.85, 58.64) * mm});
            skPoint(sketch, "E271.visualSharp", {"position": v(62.42, 59.25) * mm});
            skPoint(sketch, "E272.visualSharp", {"position": v(63.05, 58.35) * mm});
            skArc(sketch, "E272.filletArc", {"start": v(62.94, 57.93) * mm, "mid": v(62.98, 58.3) * mm, "end": v(62.85, 58.64) * mm});
            skArc(sketch, "E273.filletArc", {"start": v(62.63, 58.95) * mm, "mid": v(62.33, 59.2) * mm, "end": v(61.95, 59.27) * mm});
            skLineSegment(sketch, "E274", {"start": v(59.19, 58.03) * mm, "end": v(61, 55.64) * mm});
            skEllipticalArc(sketch, "E275.MirrorCS", {});
            skArc(sketch, "E276.MirrorCS", {"start": v(23.54, 38.95) * mm, "mid": v(23.75, 38.62) * mm, "end": v(24.1, 38.43) * mm});
            skLineSegment(sketch, "E277.MirrorCS", {"start": v(23.54, 38.95) * mm, "end": v(23.43, 39.31) * mm});
            skArc(sketch, "E278.MirrorCS", {"start": v(23.56, 40.01) * mm, "mid": v(23.4, 39.68) * mm, "end": v(23.43, 39.31) * mm});
            skEllipticalArc(sketch, "E279.MirrorCS", {});
            skArc(sketch, "E280.MirrorCS", {"start": v(26.4, 57.93) * mm, "mid": v(26.36, 58.3) * mm, "end": v(26.49, 58.64) * mm});
            skLineSegment(sketch, "E281.MirrorCS", {"start": v(26.7, 58.95) * mm, "end": v(26.49, 58.64) * mm});
            skArc(sketch, "E282.MirrorCS", {"start": v(26.7, 58.95) * mm, "mid": v(27, 59.2) * mm, "end": v(27.4, 59.27) * mm});
            skEllipticalArc(sketch, "E283.MirrorCS", {});
            skArc(sketch, "E284.MirrorCS", {"start": v(26.4, 33.8) * mm, "mid": v(26.36, 33.43) * mm, "end": v(26.49, 33.08) * mm});
            skLineSegment(sketch, "E285.MirrorCS", {"start": v(26.7, 32.77) * mm, "end": v(26.49, 33.08) * mm});
            skArc(sketch, "E286.MirrorCS", {"start": v(26.7, 32.77) * mm, "mid": v(27, 32.52) * mm, "end": v(27.4, 32.45) * mm});
            skEllipticalArc(sketch, "E287.MirrorCS", {});
            skArc(sketch, "E288.MirrorCS", {"start": v(62.94, 33.8) * mm, "mid": v(62.98, 33.43) * mm, "end": v(62.85, 33.08) * mm});
            skLineSegment(sketch, "E289.MirrorCS", {"start": v(62.63, 32.77) * mm, "end": v(62.85, 33.08) * mm});
            skArc(sketch, "E290.MirrorCS", {"start": v(62.63, 32.77) * mm, "mid": v(62.33, 32.52) * mm, "end": v(61.95, 32.45) * mm});
            const initialGuessF2  = {"E193": [0.0447003424464493, 0.06485332282106121, 0.99983442728575, 0.018196648432512064, 0.0014985999971454751, 0.0035390806210883422, 2.156609723512715, 0.9748157089481566], "E199": [0.050530618511507, 0.06390913501741177, 0.9565221208926579, -0.29165978852596675, 0.0014985999971454755, 0.003539080621088343, 2.156609723512734, 0.9748157089481593], "E205": [0.05594346551724061, 0.061102215630561924, 0.819578764825096, -0.5729665332702865, 0.0014985999971454751, 0.0035390806210883422, 2.15660972351274, 0.9748157089481442], "E211": [0.06273374051225895, 0.051529183439310455, 0.3309091192338454, -0.9436626276418288, 0.0014986009166170994, 0.0035390796439407806, 2.1566089130591894, 0.9748164926285874], "E221": [0.06358579738236796, 0.04581523748948192, 0.018196648432512126, -0.99983442728575, 0.0014985999971454751, 0.0035390806210883422, 2.156609723512595, 0.9748157089481566], "E227.MirrorCS": [0.06273374051225895, 0.04018975848764572, 0.3309091192338454, 0.9436626276418288, 0.0014986009166170994, 0.0035390796439407806, 5.308368814550999, 4.126576394120397], "E231.MirrorCS": [0.03880895786678023, 0.06390913501741177, -0.9565221208926579, -0.29165978852596686, 0.0014985999971454755, 0.003539080621088343, 5.308369598231427, 4.1265755836668525], "E236.MirrorCS": [0.03339611086104662, 0.061102215630561924, -0.8195787648250958, -0.5729665332702866, 0.0014985999971454751, 0.0035390806210883422, 5.308369598231442, 4.126575583666849], "E238.MirrorCS": [0.05594346551724061, 0.030616726296394253, 0.819578764825096, 0.5729665332702865, 0.0014985999971454751, 0.0035390806210883422, 5.308369598231442, 4.126575583666849], "E244.MirrorCS": [0.050530618511507, 0.027809806909544404, 0.9565221208926579, 0.29165978852596675, 0.0014985999971454755, 0.003539080621088343, 5.308369598231427, 4.1265755836668525], "E248.MirrorCS": [0.026605835866028285, 0.051529183439310455, -0.3309091192338453, -0.9436626276418288, 0.0014986009166170994, 0.0035390796439407806, 5.308368814550999, 4.126576394120398], "E253.MirrorCS": [0.025753778995919283, 0.04581523748948192, -0.018196648432512005, -0.99983442728575, 0.0014985999971454751, 0.0035390806210883422, 5.30836959823143, 4.126575583666991], "E257.MirrorCS": [0.0447003424464493, 0.026865619105894967, 0.99983442728575, -0.018196648432512064, 0.0014985999971454751, 0.0035390806210883422, 5.30836959823143, 4.126575583666873], "E261.MirrorCS": [0.03880895786678023, 0.027809806909544404, -0.9565221208926579, 0.29165978852596686, 0.0014985999971454755, 0.003539080621088343, 2.1566097235127337, 0.9748157089481593], "E265.MirrorCS": [0.03339611086104662, 0.030616726296394253, -0.8195787648250958, 0.5729665332702866, 0.0014985999971454751, 0.0035390806210883422, 2.1566097235127373, 0.9748157089481442], "E269": [0.060092229612861495, 0.056833476704685394, 0.6024093289154234, -0.7981873216455327, 0.0014985999971819993, 0.0035390806210497915, 2.1566097234808987, 0.9748157089786922], "E275.MirrorCS": [0.026605835866028285, 0.04018975848764572, -0.3309091192338453, 0.9436626276418288, 0.0014986009166170994, 0.0035390796439407806, 2.1566089130591886, 0.9748164926285892], "E279.MirrorCS": [0.029247346765425737, 0.056833476704685394, -0.6024093289154233, -0.7981873216455329, 0.0014985999971819993, 0.0035390806210497915, 5.308369598200894, 4.1265755836986875], "E283.MirrorCS": [0.029247346765425737, 0.03488546522227078, -0.6024093289154233, 0.7981873216455329, 0.0014985999971819993, 0.0035390806210497915, 2.1566097234808987, 0.974815708978694], "E287.MirrorCS": [0.060092229612861495, 0.03488546522227078, 0.6024093289154234, 0.7981873216455327, 0.0014985999971819993, 0.0035390806210497915, 5.308369598200894, 4.1265755836986875]};
            skSetInitialGuess(sketch, initialGuessF2);
            skSolve(sketch);
        }
        {
            var Q0;
            Q0 = qSketchRegion(id + "F2", true);
            extrude(context, id + "F3", {"entities" : qUnion([Q0]), "depth" : 6.35 * mm});
        }
        {
            var Q0;
            {var subQ0=sQuery(id+"F0.wireOp",EDGE,"E66");Q0=makeQuery(id+"F0.imprint","IMPRINT",FACE,{"disambiguationData":[TD([[makeQuery(id+"F0.imprint","IMPRINT",EDGE,{"derivedFrom":subQ0}),-1.0]])]});}
            extrude(context, id + "F4", {"entities" : qUnion([Q0]), "operationType" : NewBodyOperationType.ADD, "depth" : 12.7 * mm});
        }
        {
            var Q0;
            {var subQ0=sQuery(id+"F0.wireOp",EDGE,"E7");Q0=makeQuery(id+"F0.imprint","IMPRINT",FACE,{"disambiguationData":[TD([[makeQuery(id+"F0.imprint","IMPRINT",EDGE,{"derivedFrom":subQ0}),-1.0]])]});}
            extrude(context, id + "F5", {"entities" : qUnion([Q0]), "operationType" : NewBodyOperationType.ADD, "depth" : 12.7 * mm});
        }
        {
            var Q0;
            {var subQ0=sQuery(id+"F2.wireOp",EDGE,"E226");Q0=makeQuery(id+"F2.imprint","IMPRINT",FACE,{"disambiguationData":[TD([[makeQuery(id+"F2.imprint","IMPRINT",EDGE,{"derivedFrom":subQ0}),-1.0]])]});}
            var Q1;
            {var subQ0=sQuery(id+"F2.wireOp",EDGE,"E216");Q1=makeQuery(id+"F2.imprint","IMPRINT",FACE,{"disambiguationData":[TD([[makeQuery(id+"F2.imprint","IMPRINT",EDGE,{"derivedFrom":subQ0}),-1.0]])]});}
            extrude(context, id + "F6", {"entities" : qUnion([Q0, Q1]), "operationType" : NewBodyOperationType.ADD, "depth" : 6.35 * mm});
        }
        {
            var Q0;
            {var subQ0=sQuery(id+"F2.wireOp",EDGE,"E226");Q0=makeQuery(id+"F2.imprint","IMPRINT",FACE,{"disambiguationData":[TD([[makeQuery(id+"F2.imprint","IMPRINT",EDGE,{"derivedFrom":subQ0}),-1.0]])]});}
            extrude(context, id + "F7", {"entities" : qUnion([Q0]), "operationType" : NewBodyOperationType.ADD, "depth" : 6.35 * mm});
        }
        {
            var Q0;
            {var subQ0=sQuery(id+"F2.wireOp",EDGE,"E226");Q0=makeQuery(id+"F2.imprint","IMPRINT",FACE,{"disambiguationData":[TD([[makeQuery(id+"F2.imprint","IMPRINT",EDGE,{"derivedFrom":subQ0}),-1.0]])]});}
            extrude(context, id + "F8", {"entities" : qUnion([Q0]), "operationType" : NewBodyOperationType.ADD, "depth" : 6.35 * mm});
        }
        {
            var Q0;
            {var subQ0=sQuery(id+"F2.wireOp",EDGE,"E274");Q0=makeQuery(id+"F2.imprint","IMPRINT",FACE,{"disambiguationData":[TD([[makeQuery(id+"F2.imprint","IMPRINT",EDGE,{"derivedFrom":subQ0}),-1.0]])]});}
            extrude(context, id + "F9", {"entities" : qUnion([Q0]), "operationType" : NewBodyOperationType.ADD, "depth" : 6.35 * mm});
        }
    });
